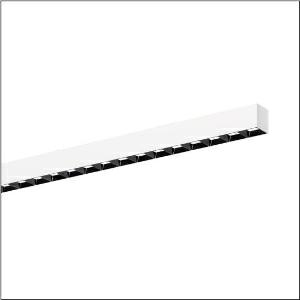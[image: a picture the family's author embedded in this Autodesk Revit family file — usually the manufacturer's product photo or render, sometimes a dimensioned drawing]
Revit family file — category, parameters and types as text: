
# Revit family: silica_r__21_51mx22tat4w_9510
name_source: partatom
category: Lighting Fixtures
units: mm (PartAtom-declared; Revit-internal decimal feet)

## family parameters
Cut with Voids When Loaded = No
Host = Face
Light Source = No
Part Type = Normal
Room Calculation Point = No
Round Connector Dimension = Use Diameter
Shared = No

## types (1)
- --- (1 x LED, 3720 lm, 32.1 W, 6500K)
    Apparent Load = 32 VA
    CIE Flux Codes = 84 100 100 100 100
    Color Rendering = 80
    Color Temperature = 6500K
    Default Elevation = 1800 mm
    Description = Silica® 21, office luminaire, primary light control with darklight reflector, of PMMA, black, CAT 2 (L<= 3000cd/m²), light emission: direct distribution, primary light characteristic: symmetric, installation type: surface-mounted, LED, rated luminous flux: 3.720lm, luminous efficacy: 110lm/W, light colour: 8tw, colour temperature: 2700..6500K, control gear: ECG DALI, with terminal, 3+2-pole, max. 2.5mm², mains connection: 220..240V, AC, 50/60Hz, rated input power: 33.8W, luminaire housing, of aluminium, traffic white (RAL 9016), length: 1.204mm, width: 53mm, height: 53mm, protection rating (complete): IP20, insulation class (complete): insulation class I (protective earthing), certification: CE, permissible operating ambient temperature: 0..+35°C, standard: EN 50419, packaging unit: 1 piece
    Height = 0 mm  [stored 0 ft]
    Lamp = 1 x LED
    Lamp Light Flux = 3720 lm
    Lamp Power = 32.1 W
    Lamp count = 1
    Length = 1204 mm
    Luminous efficacy = 116 lm/W
    Manufacturer = Siteco
    ModVariant = No
    Model = 51MX22TAT4W
    Mounting Place = Ceiling
    Mounting Type = Recessed
    Number of Poles = 1
    OnlyDefault = Yes
    Power Factor = 1
    Product Name = Silica® 21
    Product group = office luminaire | ceiling recessed
    ProductGroupID = 401
    Protection Class = Protection class I
    Protection Degree = IP 20
    RLX_Detail_Level = 1
    RLX_Emergency_Light_Flux = 0 lm
    RLX_Emergency_Type = 0
    RLX_Emergency_Type_DB = No
    RlxData = <blob elided: 37913 chars, md5=565e59aa>
    Socket = socket
    Standby Power = 0 W
    System Light Flux = 3720 lm
    System Power = 32 W
    Type Comments = individual setting
    Type Image = l_1313592.jpg
    URL = http://relux.com
    VarID = @adj_089529
    Voltage = 0 V
    Weight = 0.00 kg
    Width = 53 mm

note: [stored X ft] marks values corroborated as IEEE doubles in the binary element streams (Revit-internal decimal feet)

## geometry (parser evidence)
native form markers: Blend x4, Sweep x10
no freeform markers — native parametric forms only
